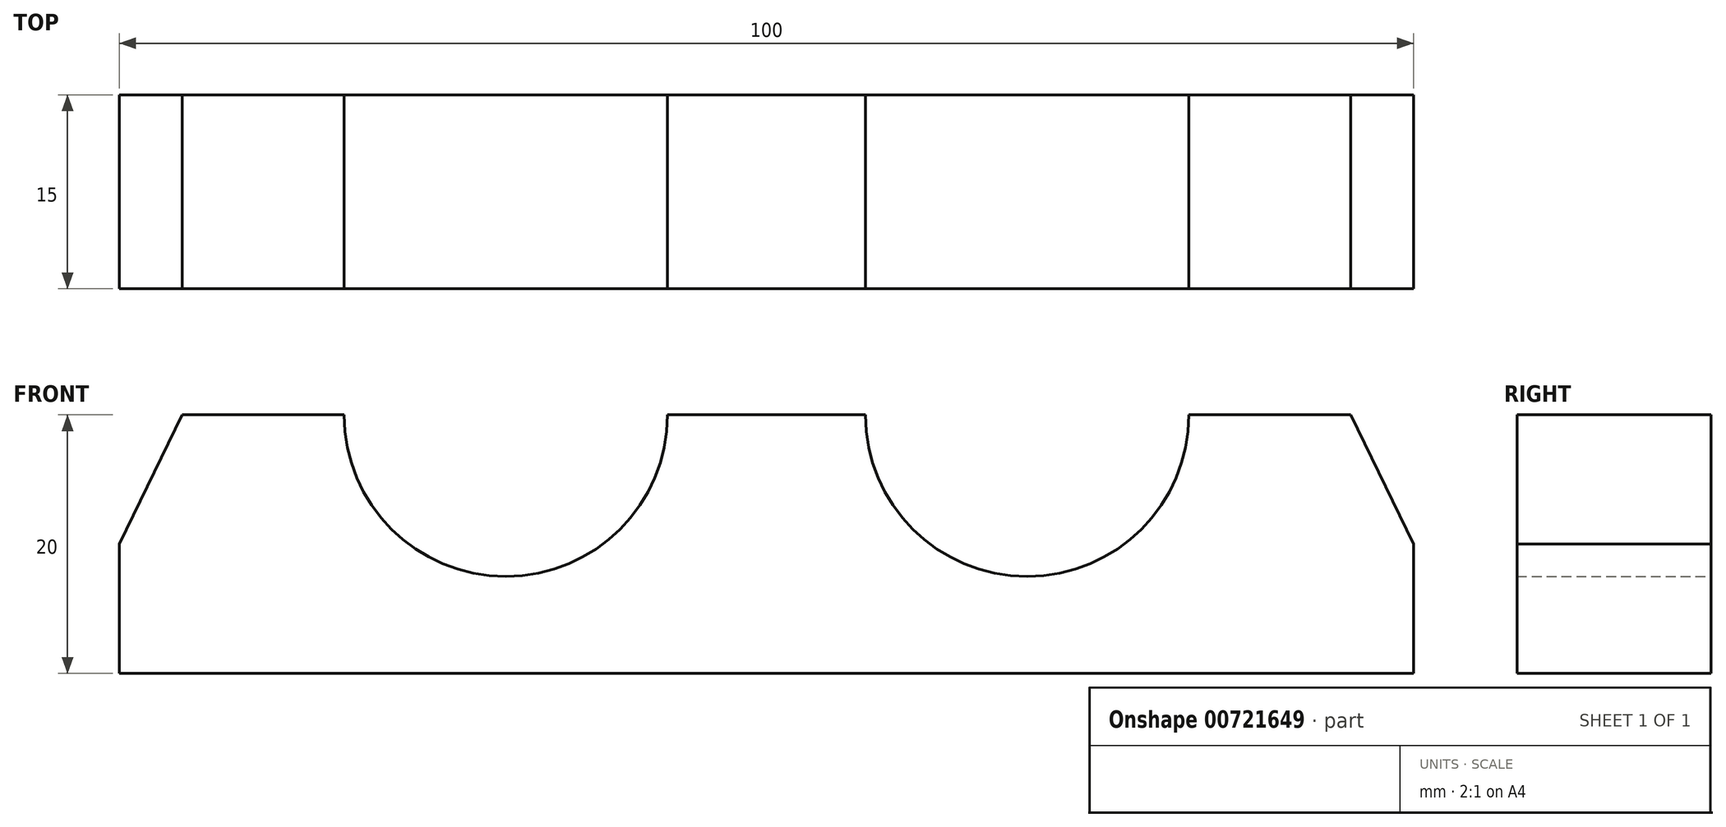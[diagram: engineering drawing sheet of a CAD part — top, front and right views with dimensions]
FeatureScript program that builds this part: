
annotation { "Feature Type Name" : "Feature", "Feature Type Description" : "" }
export const myFeature = defineFeature(function(context is Context, id is Id, definition is map)
    precondition{}
    {
        {
            var Q0;
            Q0=qCreatedBy(makeId("Front.planeOp"),FACE);
            var sketch = newSketch(context, id + "F0", { "sketchPlane" : qUnion([Q0])});
            skLineSegment(sketch, "E0", {"start": v(-19.09, 0) * mm, "end": v(80.91, 0) * mm});
            skLineSegment(sketch, "E1", {"start": v(80.91, 0) * mm, "end": v(80.91, 10) * mm});
            skLineSegment(sketch, "E2", {"start": v(-19.09, 10) * mm, "end": v(-19.09, 0) * mm});
            skLineSegment(sketch, "E3", {"start": v(-19.09, 10) * mm, "end": v(-14.23, 20) * mm});
            skLineSegment(sketch, "E4", {"start": v(-14.23, 20) * mm, "end": v(76.06, 20) * mm});
            skLineSegment(sketch, "E5", {"start": v(76.06, 20) * mm, "end": v(80.91, 10) * mm});
            skCircle(sketch, "E6", {"center": v(10.77, 20) * mm, "radius": 12.5 * mm});
            skCircle(sketch, "E7", {"center": v(51.06, 20) * mm, "radius": 12.5 * mm});
            skSolve(sketch);
        }
        {
            var Q0;
            Q0=makeQuery(id+"F0.imprint","IMPRINT",FACE,{"disambiguationData":[TD([[makeQuery(id+"F0.imprint","IMPRINT",EDGE,{"derivedFrom":sQuery(id+"F0.wireOp",EDGE,"E0")}),1.0]])]});
            extrude(context, id + "F1", {"entities" : qUnion([Q0]), "depth" : 15 * mm, "offsetDistance" : 25 * mm});
        }
    });
